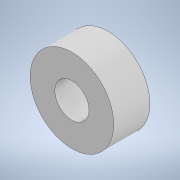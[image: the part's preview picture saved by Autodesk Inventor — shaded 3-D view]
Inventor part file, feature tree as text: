
AUTODESK INVENTOR PART (.ipt)
format: ipt  version: 2021 (Build 250183000, 183)  size: 96,768 bytes
history: native  units: mm
features: extrude x1, sketch x1
ambient origin geometry x8: Origin, YZ Plane, XZ Plane, XY Plane, X Axis, Y Axis, Z Axis, Center Point
bodies: Solid1 (feature_tree)
feature tree (2):
  extrude  "Extrusion1"  Depth=9.5mm
  sketch  "Sketch1"  dims[d0=9.0mm d1=22.0mm d2=9.5mm d3=0.0mm]
